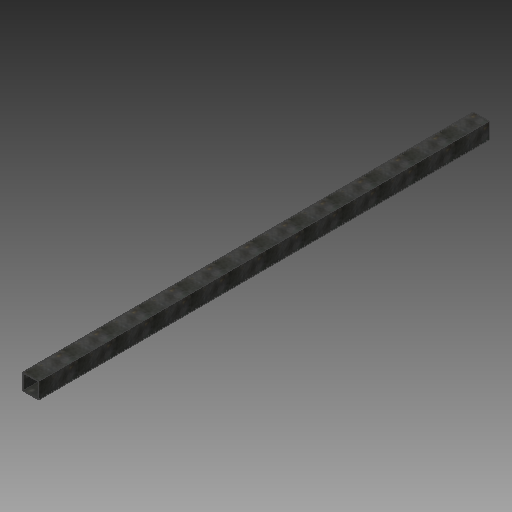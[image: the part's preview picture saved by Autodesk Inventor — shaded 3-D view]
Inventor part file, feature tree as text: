
AUTODESK INVENTOR PART (.ipt)
format: ipt  version: 2018 (Build 220112000, 112)  size: 113,664 bytes
history: native  units: mm
features: other x1, extrude x1, sketch x1
ambient origin geometry x8: Origin, YZ Plane, XZ Plane, XY Plane, X Axis, Y Axis, Z Axis, Center Point
bodies: Body1 (feature_tree)
feature tree (3):
  other  "Sólido1"
  extrude  "Extrusión1"  Depth=75.0mm
  sketch  "Boceto1"  dims[d0=75.0mm d1=75.0mm d2=3.0mm d3=37.5mm d4=37.5mm d5=2100.0mm d6=0.0mm d7=1050.0mm d8=0.0mm]
